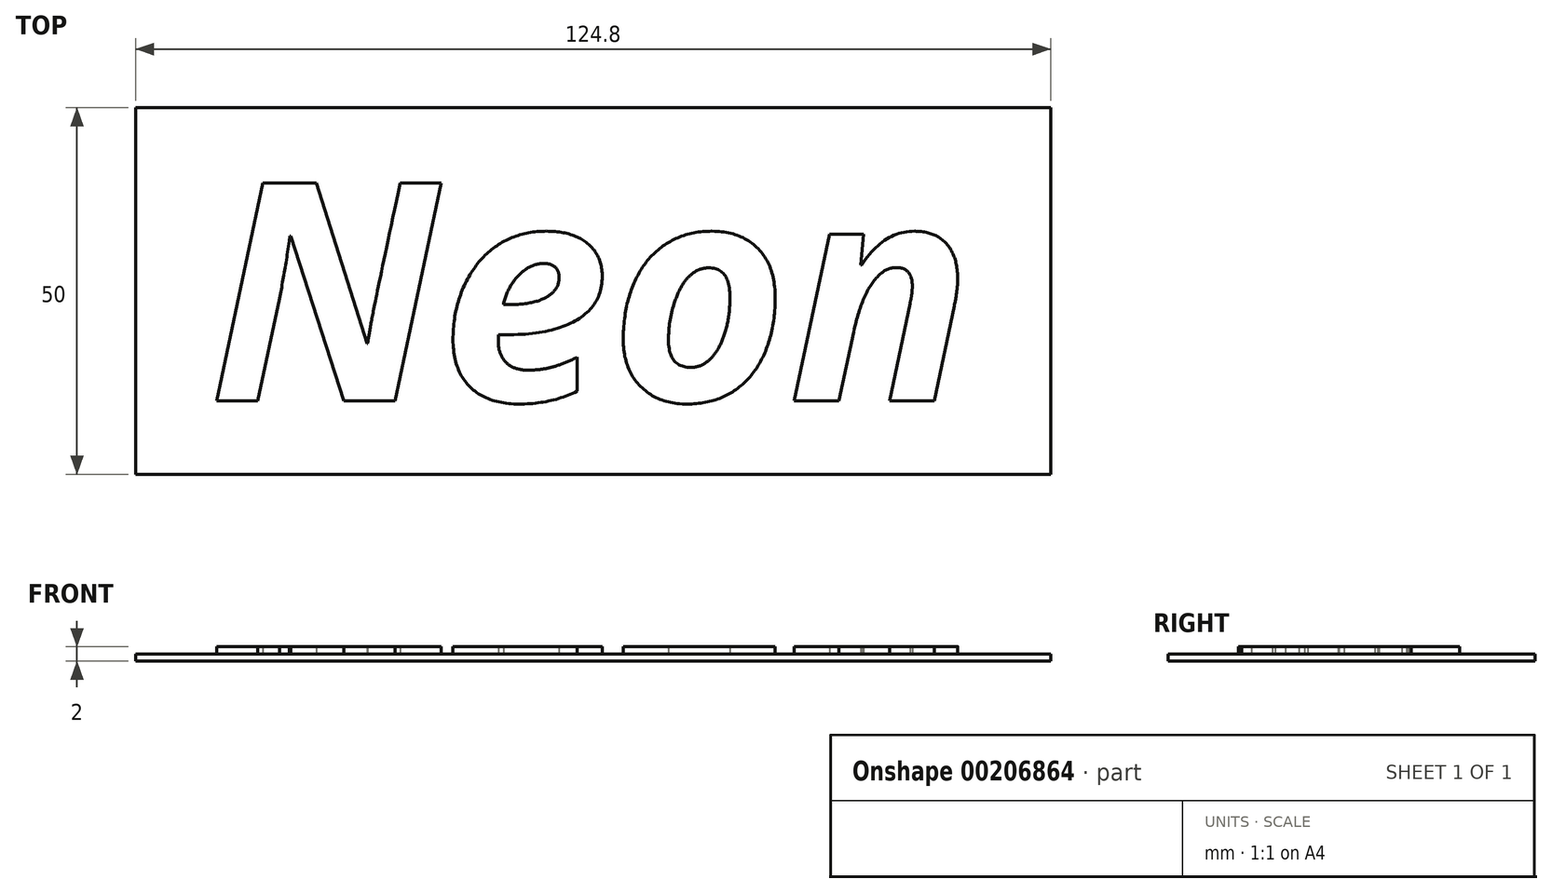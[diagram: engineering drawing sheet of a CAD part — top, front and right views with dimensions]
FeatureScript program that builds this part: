
annotation { "Feature Type Name" : "Feature", "Feature Type Description" : "" }
export const myFeature = defineFeature(function(context is Context, id is Id, definition is map)
    precondition{}
    {
        {
            var Q0;
            Q0=qCreatedBy(makeId("Top.planeOp"),FACE);
            var sketch = newSketch(context, id + "F0", { "sketchPlane" : qUnion([Q0])});
            skText(sketch, "E0", { "text": "Neon", "fontName": "OpenSans-BoldItalic.ttf"});
            const initialGuessF0  = {"E0": [0, 0, 1, 0, 0.03]};
            skSetInitialGuess(sketch, initialGuessF0);
            skSolve(sketch);
        }
        {
            var Q0;
            Q0=qCreatedBy(makeId("Top.planeOp"),FACE);
            var sketch = newSketch(context, id + "F1", { "sketchPlane" : qUnion([Q0])});
            skLineSegment(sketch, "E1.0", {"start": v(0, 0) * mm, "end": v(104.8, 0) * mm, "construction": true});
            skLineSegment(sketch, "E2.0", {"start": v(0, 0) * mm, "end": v(0, 30) * mm, "construction": true});
            skLineSegment(sketch, "E3.0", {"start": v(0, 30) * mm, "end": v(104.8, 30) * mm, "construction": true});
            skLineSegment(sketch, "E4.0", {"start": v(104.8, 0) * mm, "end": v(104.8, 30) * mm, "construction": true});
            skLineSegment(sketch, "E5.0", {"start": v(-10, 40) * mm, "end": v(114.8, 40) * mm});
            skLineSegment(sketch, "E5.1", {"start": v(-10, -10) * mm, "end": v(-10, 40) * mm});
            skLineSegment(sketch, "E5.2", {"start": v(-10, -10) * mm, "end": v(114.8, -10) * mm});
            skLineSegment(sketch, "E5.3", {"start": v(114.8, -10) * mm, "end": v(114.8, 40) * mm});
            skSolve(sketch);
        }
        {
            var Q0;
            Q0 = qSketchRegion(id + "F1", true);
            extrude(context, id + "F2", {"entities" : qUnion([Q0]), "oppositeDirection" : true, "depth" : 1 * mm});
        }
        {
            var Q0;
            Q0 = qSketchRegion(id + "F0", true);
            extrude(context, id + "F3", {"entities" : qUnion([Q0]), "operationType" : NewBodyOperationType.ADD, "depth" : 1 * mm});
        }
    });
